# Revit family: Accesories-Teknion-CEAOB-Organizer_Utility_Box-Expansion_Casework+-R2023
name_source: partatom
category: Furniture
units: mm (PartAtom-declared; Revit-internal decimal feet)

## family parameters
Always vertical = Yes
Cut with Voids When Loaded = No
Enable Cutting in Views = No
OmniClass Number = 23.40.20.00
OmniClass Title = General Furniture and Specialties
Render Appearance Source = Family Geometry
Room Calculation Point = No
Shared = Yes
Work Plane-Based = No

## types (2) — shared parameters
Assembly Code = E2020200
Description = Drawer Organizer - Utility Box - Width 6Inches
Height = 63 "
Manufacturer = Teknion
Manufacturer Fax = 416.661.4586
Part Number = CEAOB
Product Documentation Link = http://www.teknion.com
Product Line = Casework +
Product Page URL = https://www.teknion.com
Series = Expansion
Sustainability Data = https://www.teknion.com
URL = www.teknion.com
Unit Weight URL = http://www.teknion.com
Warranty = http://www.teknion.com
zero-valued in all types: Default Elevation, Length, Width

## per-type parameters (varying)
| type | 16 | 20 | Depth | Model | dIV |
| 20 - Undermount (Soft Close) | No | Yes | 18 " | CEAOB2006 | 5.982 " |
| 16 - Standard (Soft Close) | Yes | No | 15 " | CEAOB1606 | 4.982 " |

## geometry (parser evidence)
native form markers: Sweep x2
no freeform markers — native parametric forms only
